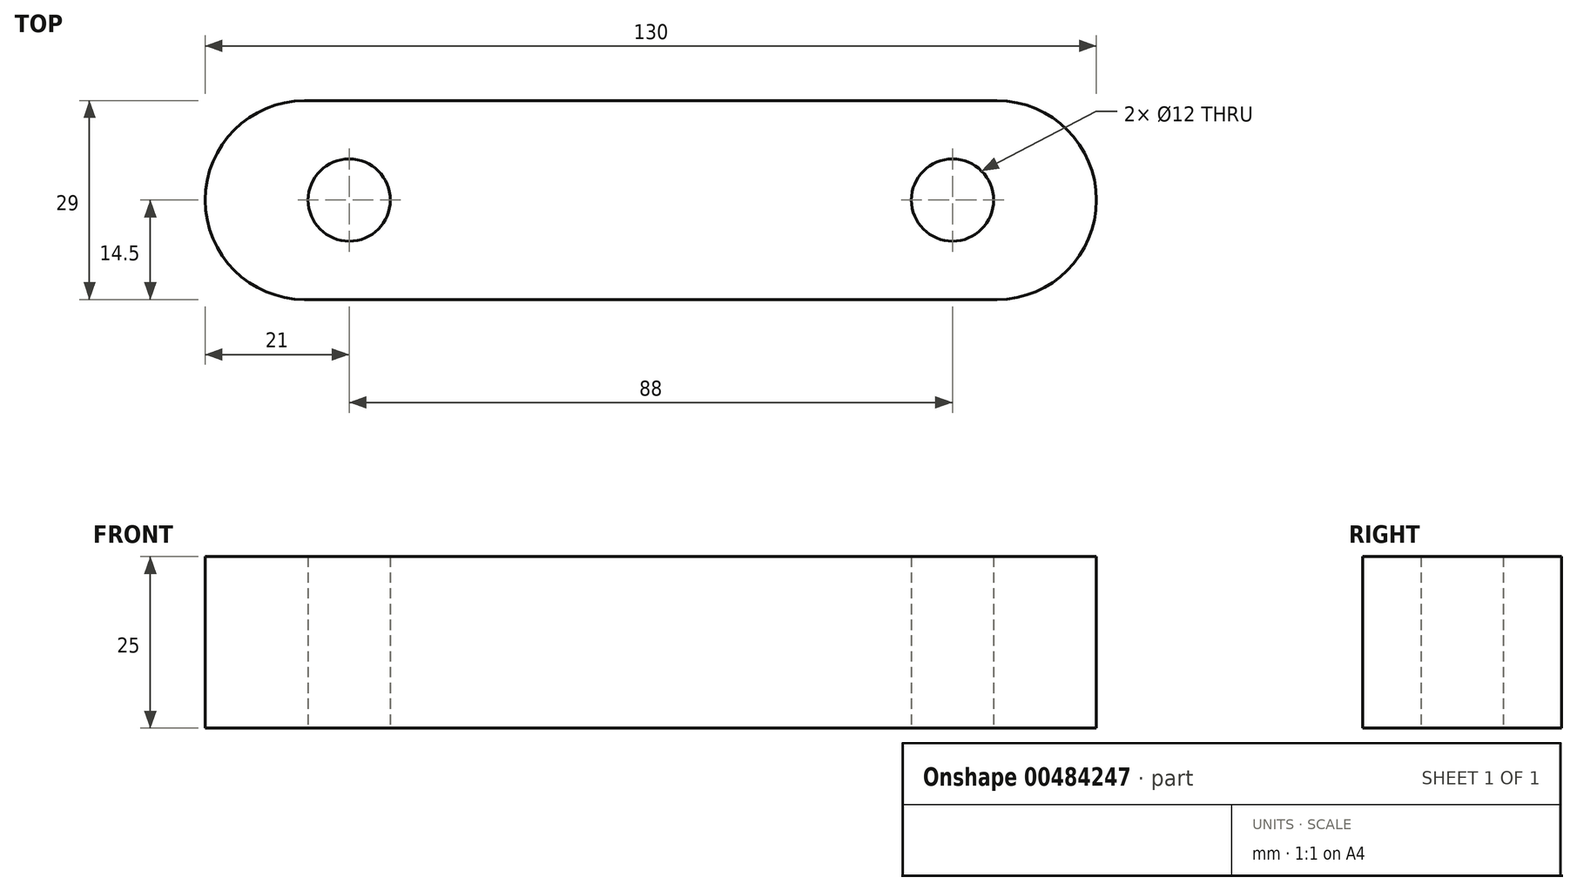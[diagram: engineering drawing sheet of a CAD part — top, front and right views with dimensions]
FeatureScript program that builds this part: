
annotation { "Feature Type Name" : "Feature", "Feature Type Description" : "" }
export const myFeature = defineFeature(function(context is Context, id is Id, definition is map)
    precondition{}
    {
        {
            var Q0;
            Q0=qCreatedBy(makeId("Top.planeOp"),FACE);
            var sketch = newSketch(context, id + "F0", { "sketchPlane" : qUnion([Q0])});
            skLineSegment(sketch, "E0", {"start": v(-50.5, 14.5) * mm, "end": v(0, 14.5) * mm});
            skLineSegment(sketch, "E1", {"start": v(0, -14.5) * mm, "end": v(-50.5, -14.5) * mm});
            skLineSegment(sketch, "E2", {"start": v(0, 14.5) * mm, "end": v(0, -14.5) * mm, "construction": true});
            skArc(sketch, "E3", {"start": v(-50.5, 14.5) * mm, "mid": v(-65, 0) * mm, "end": v(-50.5, -14.5) * mm});
            skCircle(sketch, "E4", {"center": v(-44, 0) * mm, "radius": 6 * mm});
            skCircle(sketch, "E5.MirrorC", {"center": v(44, 0) * mm, "radius": 6 * mm});
            skLineSegment(sketch, "E6.MirrorCS", {"start": v(50.5, 14.5) * mm, "end": v(0, 14.5) * mm});
            skArc(sketch, "E7.MirrorCS", {"start": v(50.5, 14.5) * mm, "mid": v(65, 0) * mm, "end": v(50.5, -14.5) * mm});
            skLineSegment(sketch, "E8.MirrorCS", {"start": v(0, -14.5) * mm, "end": v(50.5, -14.5) * mm});
            skSolve(sketch);
        }
        {
            var Q0;
            Q0=makeQuery(id+"F0.imprint","IMPRINT",FACE,{"disambiguationData":[TD([[makeQuery(id+"F0.imprint","IMPRINT",EDGE,{"derivedFrom":sQuery(id+"F0.wireOp",EDGE,"E0")}),-1.0]])]});
            extrude(context, id + "F1", {"entities" : qUnion([Q0]), "depth" : 25 * mm});
        }
    });
